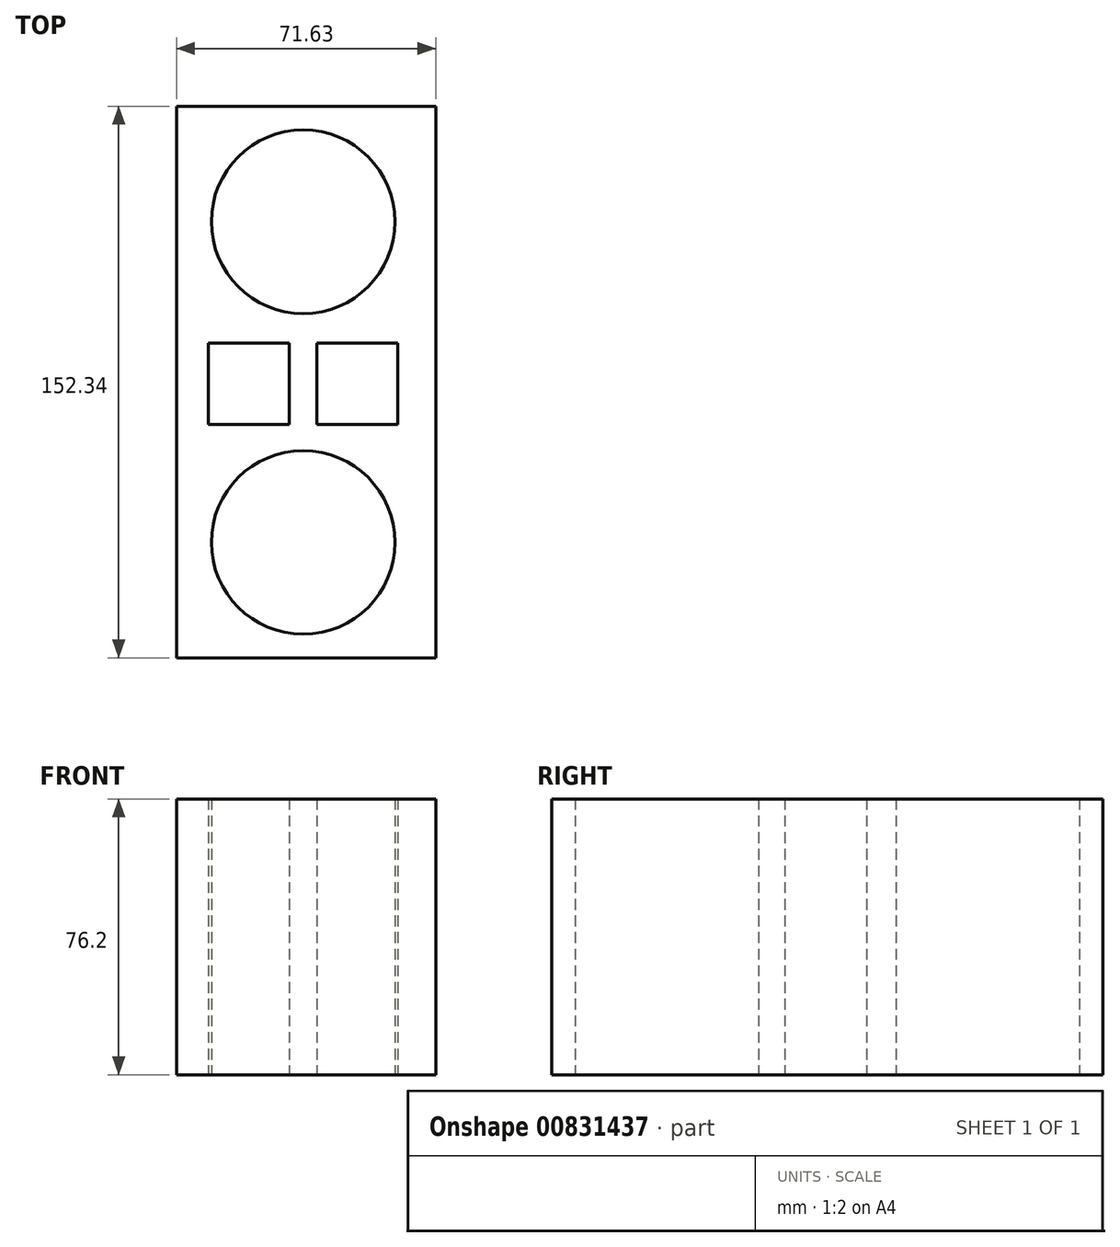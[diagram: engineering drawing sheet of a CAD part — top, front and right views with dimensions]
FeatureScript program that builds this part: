
annotation { "Feature Type Name" : "Feature", "Feature Type Description" : "" }
export const myFeature = defineFeature(function(context is Context, id is Id, definition is map)
    precondition{}
    {
        {
            var Q0;
            Q0=qCreatedBy(makeId("Top.planeOp"),FACE);
            var sketch = newSketch(context, id + "F0", { "sketchPlane" : qUnion([Q0])});
            skLineSegment(sketch, "E0.bottom", {"start": v(-35, 76.17) * mm, "end": v(36.63, 76.17) * mm});
            skLineSegment(sketch, "E0.top", {"start": v(-35, -76.17) * mm, "end": v(36.63, -76.17) * mm});
            skLineSegment(sketch, "E0.left", {"start": v(-35, 76.17) * mm, "end": v(-35, -76.17) * mm});
            skLineSegment(sketch, "E0.right", {"start": v(36.63, 76.17) * mm, "end": v(36.63, -76.17) * mm});
            skCircle(sketch, "E1", {"center": v(0, 44.3) * mm, "radius": 25.37 * mm});
            skCircle(sketch, "E2.MirrorC", {"center": v(0, -44.3) * mm, "radius": 25.37 * mm});
            skLineSegment(sketch, "E3.bottom", {"start": v(-26.17, 10.82) * mm, "end": v(-3.84, 10.82) * mm});
            skLineSegment(sketch, "E3.top", {"start": v(-26.17, -11.75) * mm, "end": v(-3.84, -11.75) * mm});
            skLineSegment(sketch, "E3.left", {"start": v(-26.17, 10.82) * mm, "end": v(-26.17, -11.75) * mm});
            skLineSegment(sketch, "E3.right", {"start": v(-3.84, 10.82) * mm, "end": v(-3.84, -11.75) * mm});
            skLineSegment(sketch, "E4.MirrorCS", {"start": v(3.84, 10.82) * mm, "end": v(3.84, -11.75) * mm});
            skLineSegment(sketch, "E5.MirrorCS", {"start": v(26.17, -11.75) * mm, "end": v(3.84, -11.75) * mm});
            skLineSegment(sketch, "E6.MirrorCS", {"start": v(26.17, 10.82) * mm, "end": v(26.17, -11.75) * mm});
            skLineSegment(sketch, "E7.MirrorCS", {"start": v(26.17, 10.82) * mm, "end": v(3.84, 10.82) * mm});
            skSolve(sketch);
        }
        {
            var Q0;
            Q0 = qSketchRegion(id + "F0", true);
            extrude(context, id + "F1", {"entities" : qUnion([Q0]), "depth" : 76.2 * mm, "offsetDistance" : 25.4 * mm});
        }
    });
